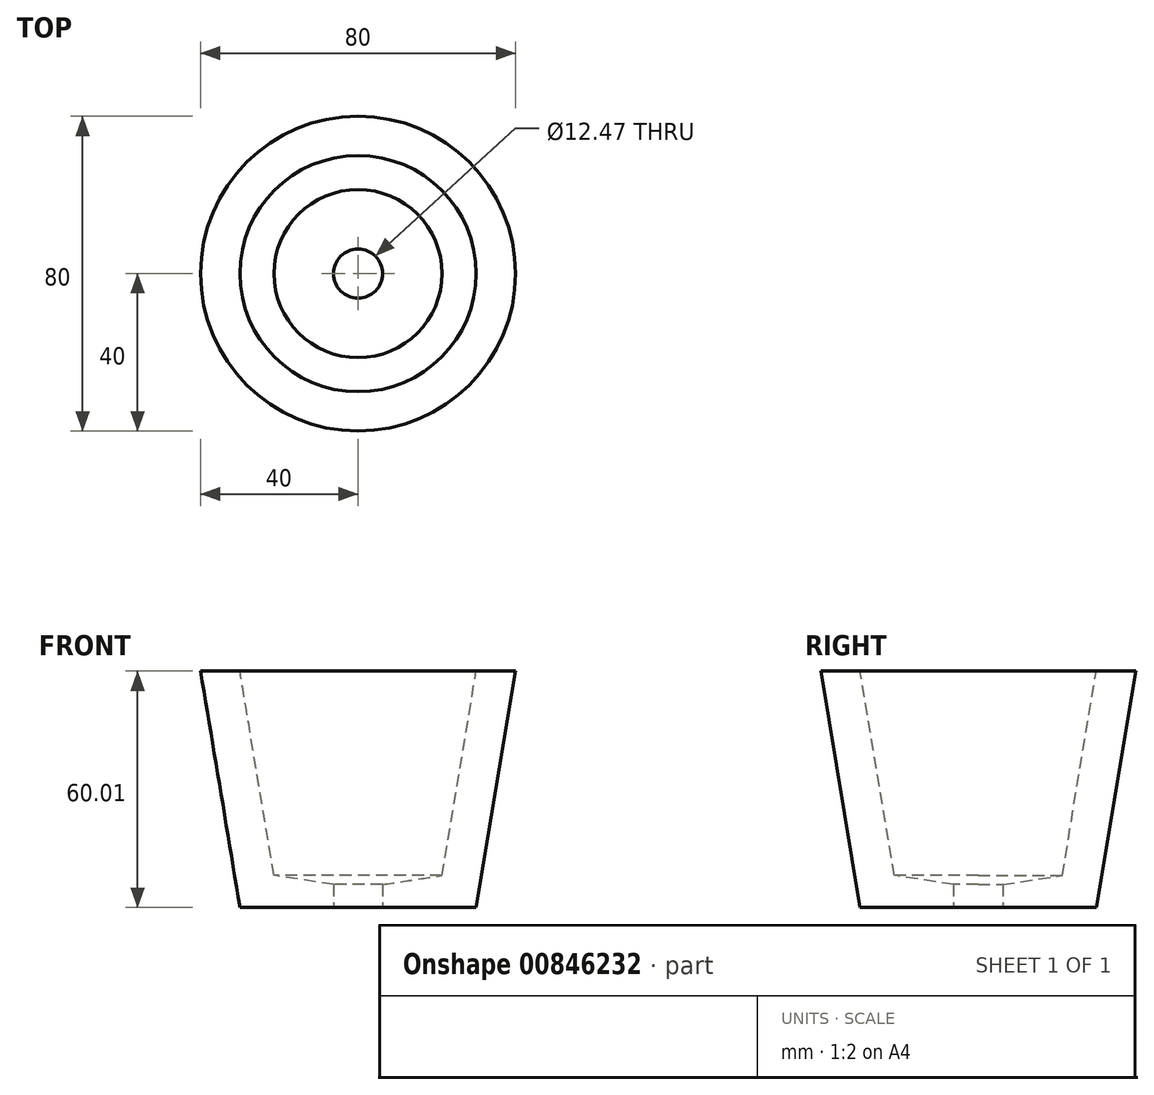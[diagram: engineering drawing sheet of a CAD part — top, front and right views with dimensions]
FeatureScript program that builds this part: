
annotation { "Feature Type Name" : "Feature", "Feature Type Description" : "" }
export const myFeature = defineFeature(function(context is Context, id is Id, definition is map)
    precondition{}
    {
        {
            var Q0;
            Q0=qCreatedBy(makeId("Front.planeOp"),FACE);
            var sketch = newSketch(context, id + "F0", { "sketchPlane" : qUnion([Q0])});
            skLineSegment(sketch, "E0", {"start": v(0, 0) * mm, "end": v(-30, 0) * mm});
            skLineSegment(sketch, "E1", {"start": v(-30, 0) * mm, "end": v(-40, 60) * mm});
            skLineSegment(sketch, "E2", {"start": v(-40, 60) * mm, "end": v(-30, 60) * mm});
            skLineSegment(sketch, "E3", {"start": v(-30, 60) * mm, "end": v(-21.35, 8.08) * mm});
            skLineSegment(sketch, "E4", {"start": v(-21.35, 8.08) * mm, "end": v(0, 4.88) * mm});
            skLineSegment(sketch, "E5", {"start": v(0, 0) * mm, "end": v(0, 4.88) * mm});
            skSolve(sketch);
        }
        {
            var Q0;
            Q0=makeQuery(id+"F0.imprint","IMPRINT",FACE,{"disambiguationData":[TD([[makeQuery(id+"F0.imprint","IMPRINT",EDGE,{"derivedFrom":sQuery(id+"F0.wireOp",EDGE,"E0")}),-1.0]])]});
            var Q1;
            Q1=sQuery(id+"F0.wireOp",EDGE,"E5");
            revolve(context, id + "F1", {"surfaceOperationType" : NewSurfaceOperationType.NEW, "entities" : qUnion([Q0]), "axis" : qUnion([Q1]), "revolveType" : RevolveType.FULL});
        }
        {
            var Q0;
            Q0=makeQuery(id+"F1.opRevolve","SWEPT_FACE",FACE,{"disambiguationData":[OSD([sQuery(id+"F0.wireOp",EDGE,"E0")])]});
            var sketch = newSketch(context, id + "F2", { "sketchPlane" : qUnion([Q0])});
            skCircle(sketch, "E6", {"center": v(0, 0) * mm, "radius": 6.23 * mm});
            skSolve(sketch);
        }
        {
            var Q0;
            Q0 = qSketchRegion(id + "F2", true);
            extrude(context, id + "F3", {"entities" : qUnion([Q0]), "operationType" : NewBodyOperationType.REMOVE, "endBound" : BoundingType.THROUGH_ALL, "oppositeDirection" : true, "depth" : 25 * mm, "offsetDistance" : 25 * mm});
        }
    });
